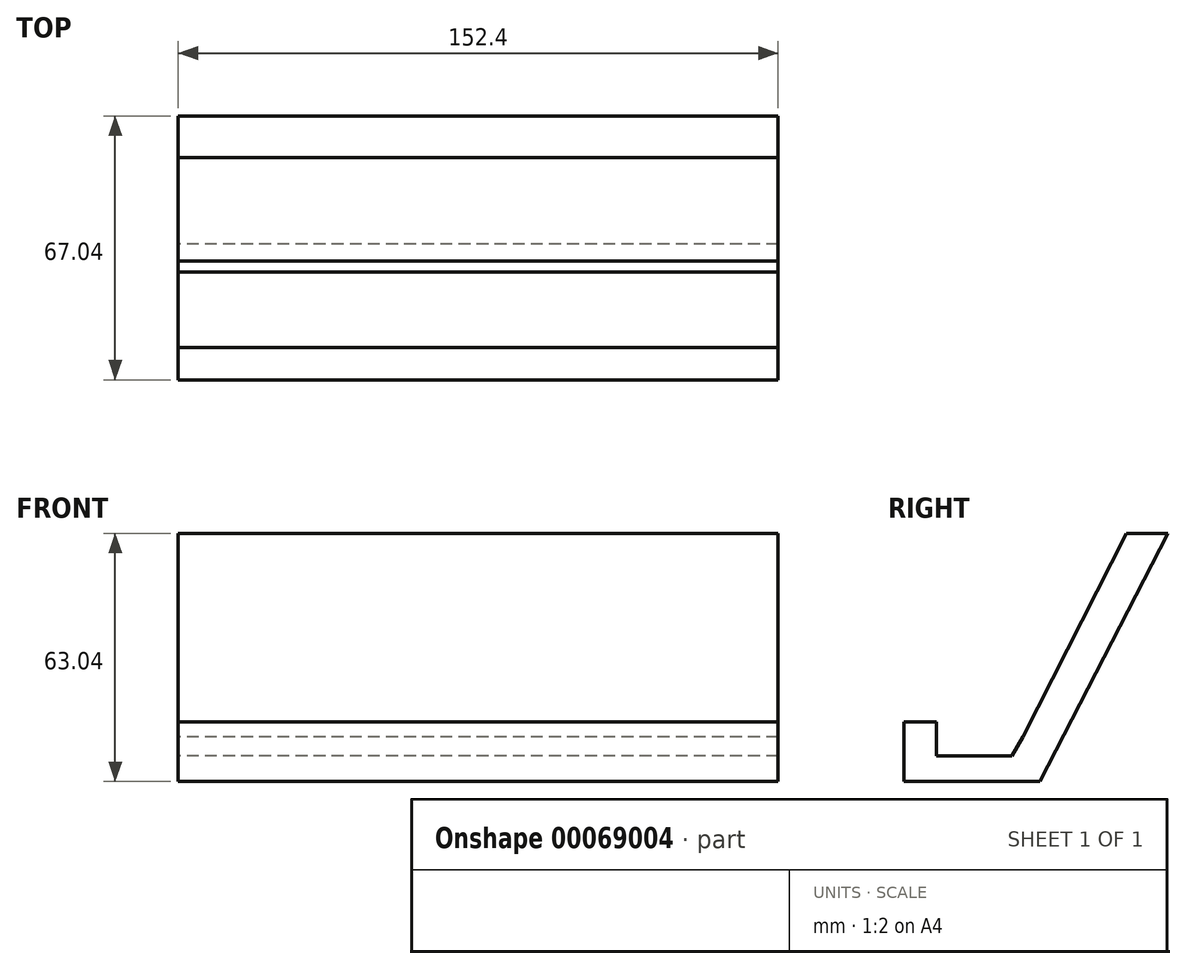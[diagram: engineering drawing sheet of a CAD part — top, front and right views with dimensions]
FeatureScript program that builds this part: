
annotation { "Feature Type Name" : "Feature", "Feature Type Description" : "" }
export const myFeature = defineFeature(function(context is Context, id is Id, definition is map)
    precondition{}
    {
        {
            var Q0;
            Q0=qCreatedBy(makeId("Right.planeOp"),FACE);
            var sketch = newSketch(context, id + "F0", { "sketchPlane" : qUnion([Q0])});
            skLineSegment(sketch, "E0", {"start": v(0, 0) * mm, "end": v(26.24, 51.77) * mm});
            skLineSegment(sketch, "E1", {"start": v(26.24, 51.77) * mm, "end": v(36.8, 51.77) * mm});
            skLineSegment(sketch, "E2", {"start": v(36.8, 51.77) * mm, "end": v(4.28, -11.27) * mm});
            skLineSegment(sketch, "E3", {"start": v(4.28, -11.27) * mm, "end": v(-30.24, -11.27) * mm});
            skLineSegment(sketch, "E4", {"start": v(-30.24, -11.27) * mm, "end": v(-30.24, 3.85) * mm});
            skLineSegment(sketch, "E5", {"start": v(-30.24, 3.85) * mm, "end": v(-21.96, 3.85) * mm});
            skLineSegment(sketch, "E6", {"start": v(-21.96, 3.85) * mm, "end": v(-21.96, -4.7) * mm});
            skLineSegment(sketch, "E7", {"start": v(-21.96, -4.7) * mm, "end": v(-2.85, -4.7) * mm});
            skLineSegment(sketch, "E8", {"start": v(-2.85, -4.7) * mm, "end": v(0, 0) * mm});
            skSolve(sketch);
        }
        {
            var Q0;
            Q0 = qSketchRegion(id + "F0", true);
            extrude(context, id + "F1", {"entities" : qUnion([Q0]), "depth" : 76.2 * mm, "hasSecondDirection" : true, "secondDirectionOppositeDirection" : true, "secondDirectionDepth" : 76.2 * mm});
        }
    });
